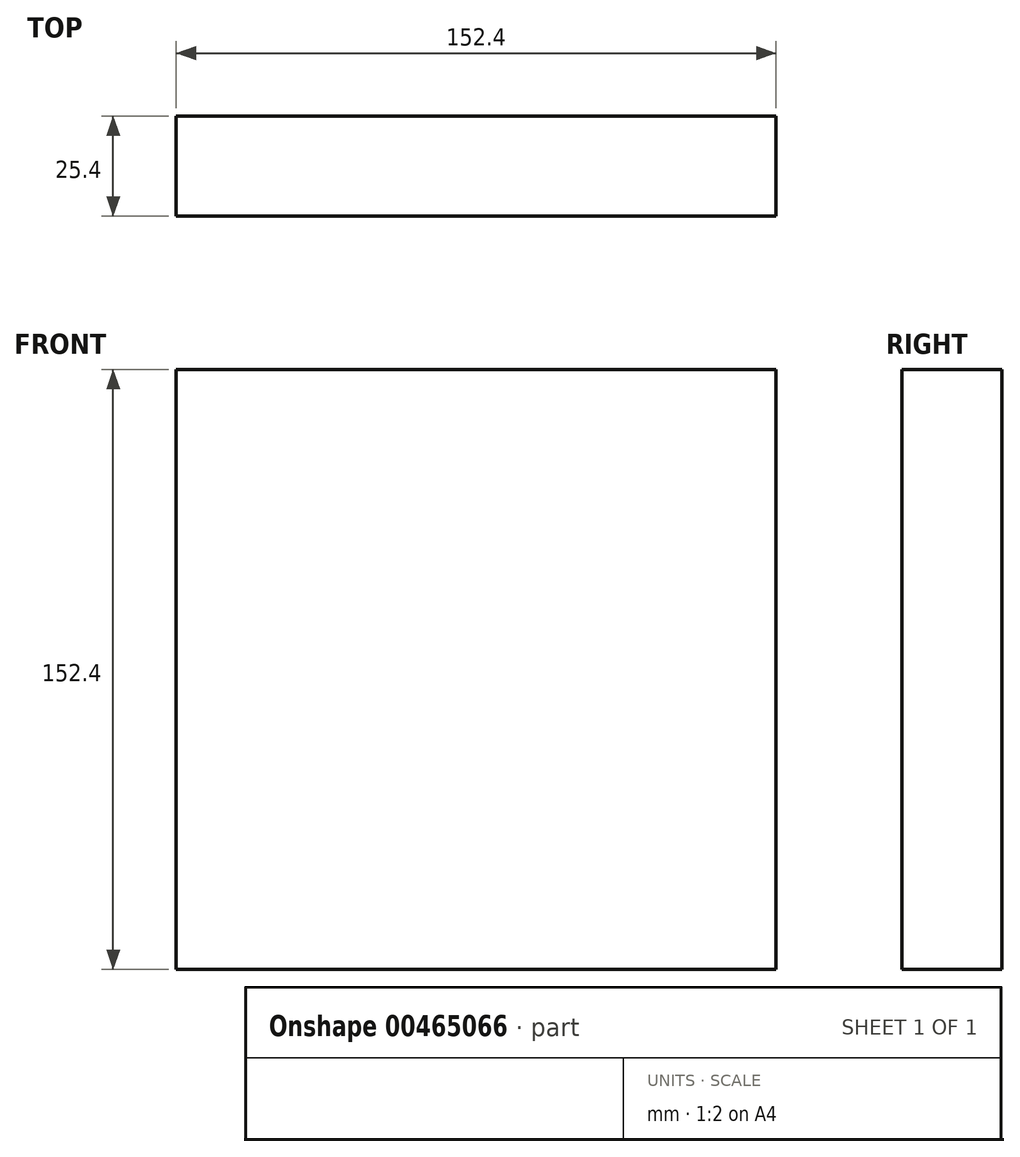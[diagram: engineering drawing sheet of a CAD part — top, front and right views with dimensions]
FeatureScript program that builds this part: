
annotation { "Feature Type Name" : "Feature", "Feature Type Description" : "" }
export const myFeature = defineFeature(function(context is Context, id is Id, definition is map)
    precondition{}
    {
        {
            var Q0;
            Q0=qCreatedBy(makeId("Front.planeOp"),FACE);
            var sketch = newSketch(context, id + "F0", { "sketchPlane" : qUnion([Q0])});
            skLineSegment(sketch, "E0.bottom", {"start": v(-76.43, 75.93) * mm, "end": v(75.97, 75.93) * mm});
            skLineSegment(sketch, "E0.top", {"start": v(-76.43, -76.47) * mm, "end": v(75.97, -76.47) * mm});
            skLineSegment(sketch, "E0.left", {"start": v(-76.43, 75.93) * mm, "end": v(-76.43, -76.47) * mm});
            skLineSegment(sketch, "E0.right", {"start": v(75.97, 75.93) * mm, "end": v(75.97, -76.47) * mm});
            skSolve(sketch);
        }
        {
            var Q0;
            Q0 = qSketchRegion(id + "F0", true);
            extrude(context, id + "F1", {"entities" : qUnion([Q0]), "depth" : 25.4 * mm});
        }
    });
